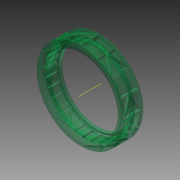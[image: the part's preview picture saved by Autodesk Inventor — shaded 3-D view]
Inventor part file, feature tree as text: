
AUTODESK INVENTOR PART (.ipt)
format: ipt  version: 2013 (Build 170138000, 138)  size: 1,973,248 bytes
history: native  units: in
note: dims shown in document units (in); Inventor stores cm internally (conversion verified against a paired STEP export)
features: sketch x11, plane x6, extrude x4, pattern_circular x3, sweep x3, revolve x1, other x1, mirror x1, fillet x1
ambient origin geometry x8: Origin, YZ Plane, XZ Plane, XY Plane, X Axis, Y Axis, Z Axis, Center Point
bodies: Solid1 (feature_tree)
feature tree (31):
  revolve  "Revolution1"  [1 undecoded]
  extrude  "Extrusion1"  Depth=0.04in
  pattern_circular  "Circular Pattern1"  [2 undecoded]
  plane  "Work Plane1"
  other  "Work Axis1"
  extrude  "Extrusion2"  Depth=0.016in
  pattern_circular  "Circular Pattern3"  [2 undecoded]
  plane  "Work Plane3"
  plane  "Work Plane5"
  extrude  "Extrusion3"  Depth=0.03in
  extrude  "Extrusion4"  Depth=0.039in
  plane  "Work Plane6"
  sweep  "Sweep1"
  plane  "Work Plane7"
  sweep  "Sweep2"
  mirror  "Mirror1"
  sketch  "Sketch11"  dims[d13=0.012in]
  plane  "Work Plane8"
  sweep  "Sweep3"
  pattern_circular  "Circular Pattern4"  [2 undecoded]
  fillet  "Fillet1"  Radius=0.038in
  sketch  "Sketch2"  dims[d2=0.439in d3=0.347in]
  sketch  "Sketch3"  dims[d4=0.006in d5=0.04in]
  sketch  "Sketch6"  dims[d7=0.079in]
  sketch  "Sketch7"  dims[d8=0.012in]
  sketch  "Sketch8"  dims[d9=0.16in]
  sketch  "Sketch9"  dims[d11=0.039in]
  sketch  "3D Sketch1"
  sketch  "Sketch10"  dims[d12=0.008in]
  sketch  "3D Sketch2"
  sketch  "Sketch12"  dims[d14=0.012in d15=0.063in d16=0.016in d17=0.016in d18=0.03in d19=0.039in d20=0.013in d21=0.012in d22=0.165in d24=0.073in d25=0.038in d26=1.618in d28=0.237in d29=0.205in d30=0.042in d31=90.0deg d32=3.66in d33=3.5in d35=0.0962in d36=11.811in d38=360.0deg d40=0.147in d41=1.83in d42=1.75in d43=0.7in d44=0.0in d45=11.811in d46=360.0deg d67=0.05in d68=0.1718in d69=0.1718in d70=0.82in d71=0.0in d72=6.2992in d73=360.0deg d79=0.15in d80=0.015in d81=0.025in d82=0.025in d83=0.025in d84=0.025in d85=0.025in d86=0.025in d88=0.82in d89=0.0in d90=4.5in d91=0.0in d92=0.0in d93=0.1718in d94=0.1718in d96=0.0in d97=0.1718in d98=0.0in d99=0.1718in d100=0.1718in d101=0.05in d102=0.01in d103=0.0in d104=3.1496in d105=360.0deg d107=0.012in]
note: 7 required parameter values undecoded (feature->parameter linkage not recoverable at this tier; creation-order binding heuristic only, values carry confidence <= 0.55)